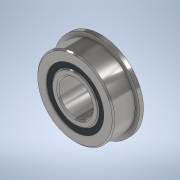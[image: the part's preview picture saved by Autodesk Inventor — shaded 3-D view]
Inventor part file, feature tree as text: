
AUTODESK INVENTOR PART (.ipt)
format: ipt  version: 2020 (Build 240168000, 168)  size: 628,736 bytes
history: native  units: in
note: dims shown in document units (in); Inventor stores cm internally (conversion verified against a paired STEP export)
features: other x11, revolve x5
ambient origin geometry x8: Origin, YZ Plane, XZ Plane, XY Plane, X Axis, Y Axis, Z Axis, Center Point
bodies: Solid1 (feature_tree), Solid2 (feature_tree), Solid3 (feature_tree), Solid4 (feature_tree), Solid5 (feature_tree), Solid6 (feature_tree), Solid7 (feature_tree), Solid8 (feature_tree), Solid9 (feature_tree), Solid10 (feature_tree), Solid11 (feature_tree), Solid12 (feature_tree), Solid13 (feature_tree), Solid14 (feature_tree), Solid15 (feature_tree), Solid16 (feature_tree)
feature tree (16):
  revolve  "Revolve3"  [1 undecoded]
  revolve  "Revolve4"  [1 undecoded]
  other  "CirPattern1[1]"
  other  "CirPattern1[2]"
  other  "CirPattern1[3]"
  other  "CirPattern1[4]"
  other  "CirPattern1[5]"
  other  "CirPattern1[6]"
  other  "CirPattern1[7]"
  other  "CirPattern1[8]"
  other  "CirPattern1[9]"
  other  "CirPattern1[10]"
  other  "CirPattern1[11]"
  revolve  "Revolve5[1]"  [1 undecoded]
  revolve  "Revolve5[2]"  [1 undecoded]
  revolve  "Revolve6"  [1 undecoded]
note: 5 required parameter values undecoded (feature->parameter linkage not recoverable at this tier; creation-order binding heuristic only, values carry confidence <= 0.55)
